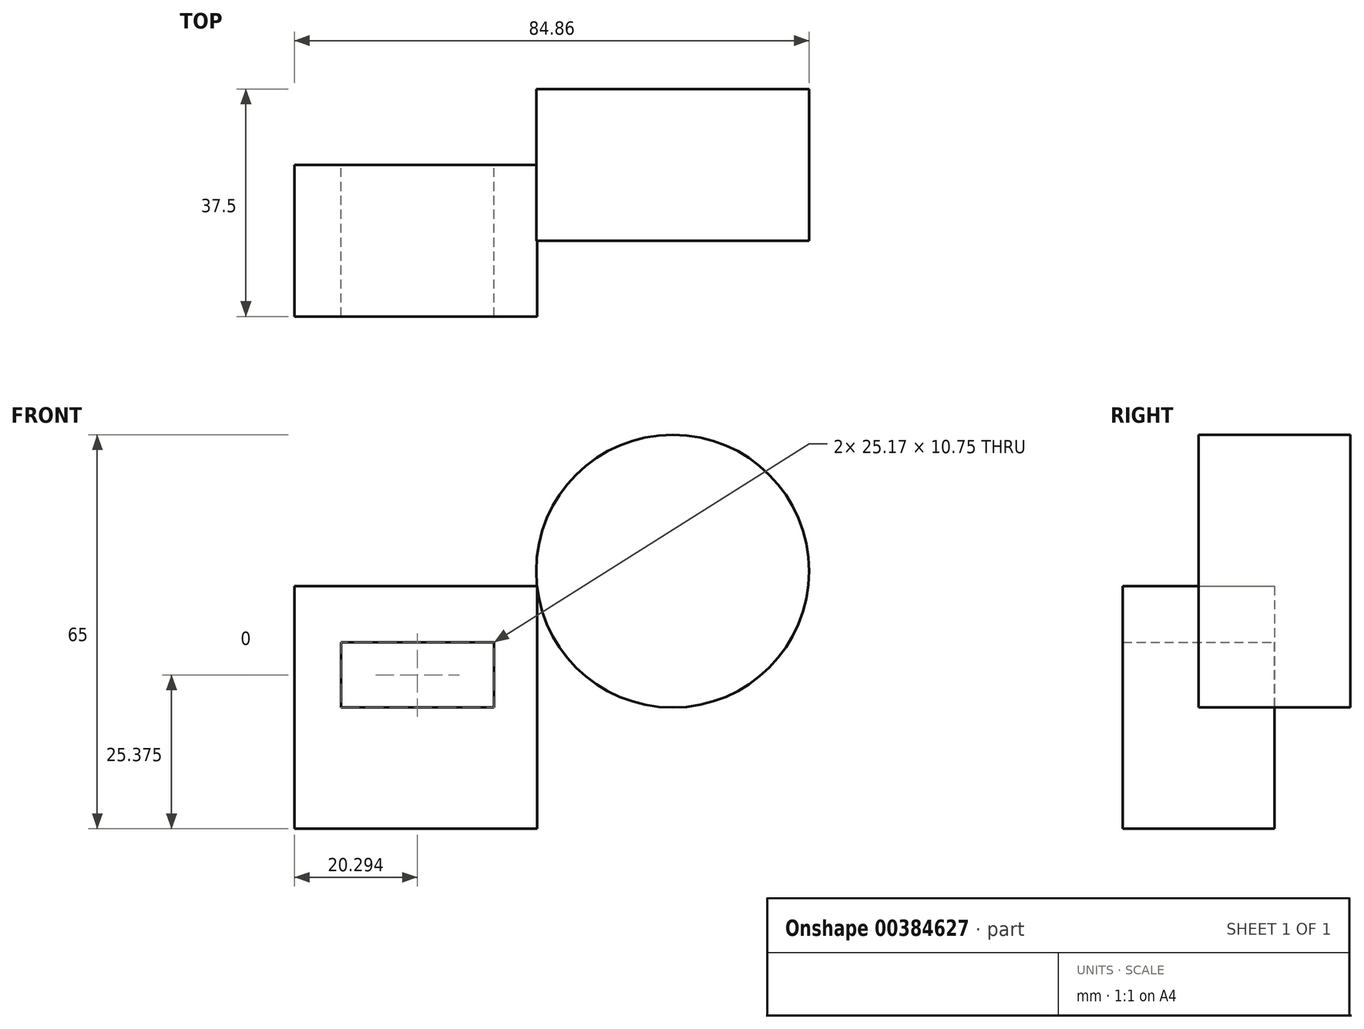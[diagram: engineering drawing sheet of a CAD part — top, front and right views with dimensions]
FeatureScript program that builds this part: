
annotation { "Feature Type Name" : "Feature", "Feature Type Description" : "" }
export const myFeature = defineFeature(function(context is Context, id is Id, definition is map)
    precondition{}
    {
        {
            var Q0;
            Q0=qCreatedBy(makeId("Front.planeOp"),FACE);
            var sketch = newSketch(context, id + "F0", { "sketchPlane" : qUnion([Q0])});
            skLineSegment(sketch, "E0.bottom", {"start": v(20, 20) * mm, "end": v(-20, 20) * mm});
            skLineSegment(sketch, "E0.top", {"start": v(20, -20) * mm, "end": v(-20, -20) * mm});
            skLineSegment(sketch, "E0.left", {"start": v(20, 20) * mm, "end": v(20, -20) * mm});
            skLineSegment(sketch, "E0.right", {"start": v(-20, 20) * mm, "end": v(-20, -20) * mm});
            skPoint(sketch, "E0.middle", {"position": v(0, 0) * mm});
            skCircle(sketch, "E1", {"center": v(42.36, 22.5) * mm, "radius": 22.5 * mm});
            skLineSegment(sketch, "E2.bottom", {"start": v(12.88, 0) * mm, "end": v(-12.29, 0) * mm});
            skLineSegment(sketch, "E2.top", {"start": v(12.88, 10.75) * mm, "end": v(-12.29, 10.75) * mm});
            skLineSegment(sketch, "E2.left", {"start": v(12.88, 0) * mm, "end": v(12.88, 10.75) * mm});
            skLineSegment(sketch, "E2.right", {"start": v(-12.29, 0) * mm, "end": v(-12.29, 10.75) * mm});
            skSolve(sketch);
        }
        {
            var Q0;
            Q0=makeQuery(id+"F0.imprint","IMPRINT",FACE,{"disambiguationData":[TD([[makeQuery(id+"F0.imprint","IMPRINT",EDGE,{"derivedFrom":sQuery(id+"F0.wireOp",EDGE,"E0.bottom")}),1.0]])]});
            extrude(context, id + "F1", {"entities" : qUnion([Q0]), "depth" : 25 * mm});
        }
        {
            var Q0;
            Q0=makeQuery(id+"F0.imprint","IMPRINT",FACE,{"disambiguationData":[TD([[makeQuery(id+"F0.imprint","IMPRINT",EDGE,{"derivedFrom":sQuery(id+"F0.wireOp",EDGE,"E1")}),1.0]])]});
            extrude(context, id + "F2", {"entities" : qUnion([Q0]), "endBound" : BoundingType.SYMMETRIC, "depth" : 25 * mm});
        }
    });
